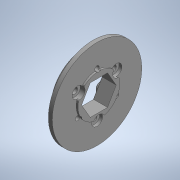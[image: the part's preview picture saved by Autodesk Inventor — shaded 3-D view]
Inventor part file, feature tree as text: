
AUTODESK INVENTOR PART (.ipt)
format: ipt  version: 2020 (Build 240168000, 168)  size: 360,448 bytes
history: native  units: mm (DEFAULTED — no unit token found)
features: chamfer x1
ambient origin geometry x8: Origin, YZ Plane, XZ Plane, XY Plane, X Axis, Y Axis, Z Axis, Center Point
bodies: Solid1 (feature_tree)
feature tree (1):
  chamfer  "Chamfer2"  [1 undecoded]
note: 1 required parameter value undecoded (feature->parameter linkage not recoverable at this tier; creation-order binding heuristic only, values carry confidence <= 0.55)
